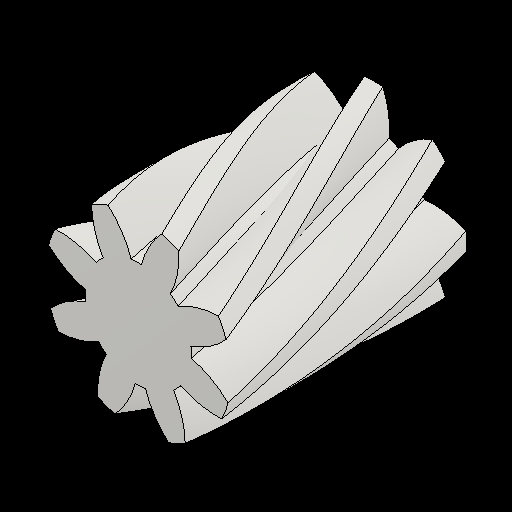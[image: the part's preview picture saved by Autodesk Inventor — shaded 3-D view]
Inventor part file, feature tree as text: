
AUTODESK INVENTOR PART (.ipt)
format: ipt  version: 2023.2 (Build 272271030, 271C)  size: 319,488 bytes
history: native  units: mm (DEFAULTED — no unit token found)
features: plane x3, other x3, sketch x2, extrude x1
ambient origin geometry x8: Origin, YZ Plane, XZ Plane, XY Plane, X Axis, Y Axis, Z Axis, Center Point
bodies: Solid1 (feature_tree)
feature tree (9):
  extrude  "Extrusion1"  Depth=20.0mm TaperAngle=0.0deg
  plane  "Work Plane2"
  plane  "Work Plane8"
  plane  "Work Plane9"
  other  "Spur Gear"
  sketch  "Sketch1"  dims[d0=15.770133mm d1=20.0mm d2=0.0mm]
  sketch  "Sketch2"  dims[d3=12.770133mm d4=10.0mm d5=0.0mm d16=12.770133mm d17=0.0mm d34=22.5deg d39=0.0mm d41=0.0mm d43=12.770133mm d46=12.770133mm d47=0.0mm d48=0.0mm]
  other  "Srf1"
  other  "Pitch Diameter"
